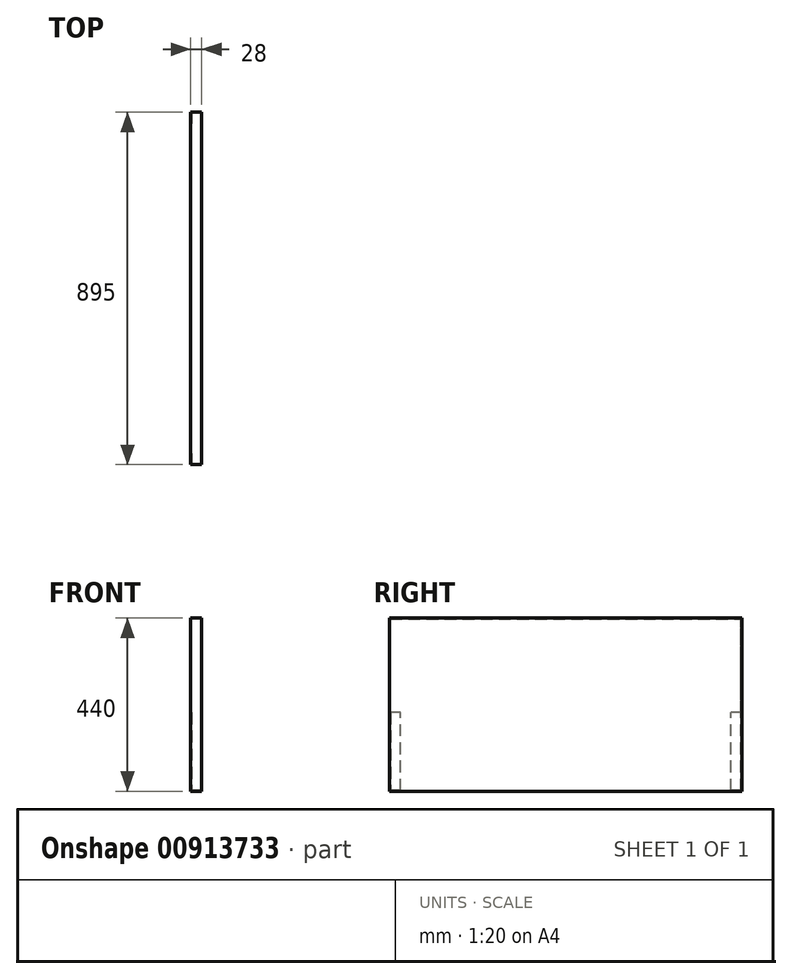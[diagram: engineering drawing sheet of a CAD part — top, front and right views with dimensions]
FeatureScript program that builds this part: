
annotation { "Feature Type Name" : "Feature", "Feature Type Description" : "" }
export const myFeature = defineFeature(function(context is Context, id is Id, definition is map)
    precondition{}
    {
        {
            var Q0;
            Q0=qCreatedBy(makeId("Right.planeOp"),FACE);
            var sketch = newSketch(context, id + "F0", { "sketchPlane" : qUnion([Q0])});
            skLineSegment(sketch, "E0.bottom", {"start": v(-447.5, -220) * mm, "end": v(447.5, -220) * mm});
            skLineSegment(sketch, "E0.top", {"start": v(-447.5, 220) * mm, "end": v(447.5, 220) * mm});
            skLineSegment(sketch, "E0.left", {"start": v(-447.5, -220) * mm, "end": v(-447.5, 220) * mm});
            skLineSegment(sketch, "E0.right", {"start": v(447.5, -220) * mm, "end": v(447.5, 220) * mm});
            skPoint(sketch, "E0.middle", {"position": v(0, 0) * mm});
            skSolve(sketch);
        }
        {
            var Q0;
            Q0 = qSketchRegion(id + "F0", true);
            extrude(context, id + "F1", {"entities" : qUnion([Q0]), "depth" : 28 * mm, "offsetDistance" : 25 * mm});
        }
        {
            var Q0;
            Q0=makeQuery(id+"F1.opExtrude","CAP_FACE",FACE,{"disambiguationData":[OSD([sQuery(id+"F0.wireOp",EDGE,"E0.bottom"),sQuery(id+"F0.wireOp",EDGE,"E0.top"),sQuery(id+"F0.wireOp",EDGE,"E0.left"),sQuery(id+"F0.wireOp",EDGE,"E0.right")])],"isStart":true});
            shell(context, id + "F2", {"entities" : qUnion([Q0]), "thickness" : 2 * mm});
        }
        {
            var Q0;
            Q0=makeQuery(id+"F1.opExtrude","CAP_FACE",FACE,{"disambiguationData":[OSD([sQuery(id+"F0.wireOp",EDGE,"E0.bottom"),sQuery(id+"F0.wireOp",EDGE,"E0.top"),sQuery(id+"F0.wireOp",EDGE,"E0.left"),sQuery(id+"F0.wireOp",EDGE,"E0.right")])],"isStart":true});
            var sketch = newSketch(context, id + "F3", { "sketchPlane" : qUnion([Q0])});
            skSolve(sketch);
        }
        {
            var Q0;
            {var subQ6=sQuery(id+"F0.wireOp",EDGE,"E0.bottom");var subQ7=makeQuery(id+"F1.opExtrude","CAP_EDGE",EDGE,{"disambiguationData":[OSD([subQ6])],"isStart":true});Q0=makeQuery(id+"F3.imprint","IMPRINT",FACE,{"disambiguationData":[TD([[makeQuery(id+"F3.imprint","IMPRINT",EDGE,{"derivedFrom":subQ7}),-1.0]])]});}
            var sketch = newSketch(context, id + "F4", { "sketchPlane" : qUnion([Q0])});
            skLineSegment(sketch, "E1.bottom", {"start": v(-447.5, -220) * mm, "end": v(-419.5, -220) * mm});
            skLineSegment(sketch, "E1.top", {"start": v(-447.5, -20) * mm, "end": v(-419.5, -20) * mm});
            skLineSegment(sketch, "E1.left", {"start": v(-447.5, -220) * mm, "end": v(-447.5, -20) * mm});
            skLineSegment(sketch, "E1.right", {"start": v(-419.5, -220) * mm, "end": v(-419.5, -20) * mm});
            skLineSegment(sketch, "E2.bottom", {"start": v(419.5, -220) * mm, "end": v(447.5, -220) * mm});
            skLineSegment(sketch, "E2.top", {"start": v(419.5, -20) * mm, "end": v(447.5, -20) * mm});
            skLineSegment(sketch, "E2.left", {"start": v(419.5, -220) * mm, "end": v(419.5, -20) * mm});
            skLineSegment(sketch, "E2.right", {"start": v(447.5, -220) * mm, "end": v(447.5, -20) * mm});
            skSolve(sketch);
        }
        {
            var Q0;
            Q0 = qSketchRegion(id + "F4", true);
            extrude(context, id + "F5", {"entities" : qUnion([Q0]), "operationType" : NewBodyOperationType.ADD, "oppositeDirection" : true, "depth" : 2 * mm, "offsetDistance" : 25 * mm});
        }
    });
